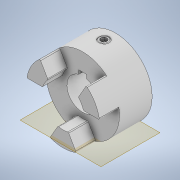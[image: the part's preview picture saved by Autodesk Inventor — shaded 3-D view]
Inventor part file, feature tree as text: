
AUTODESK INVENTOR PART (.ipt)
format: ipt  version: 2021 (Build 250183000, 183)  size: 218,624 bytes
history: native  units: in
note: dims shown in document units (in); Inventor stores cm internally (conversion verified against a paired STEP export)
features: plane x1, extrude x1, sketch x1, other x1, chamfer x1
ambient origin geometry x8: Origin, YZ Plane, XZ Plane, XY Plane, X Axis, Y Axis, Z Axis, Center Point
bodies: Solid1 (feature_tree), Solid2 (feature_tree)
feature tree (5):
  plane  "Work Plane1"
  extrude  "Extrusion1"  Depth=0.375in
  sketch  "Sketch1"  dims[d0=-0.75in d1=0.375in d2=0.5in d3=0.375in d4=0.0in]
  other  "Cut-Extrude2"
  chamfer  "Chamfer4"  Distance=0.5in
